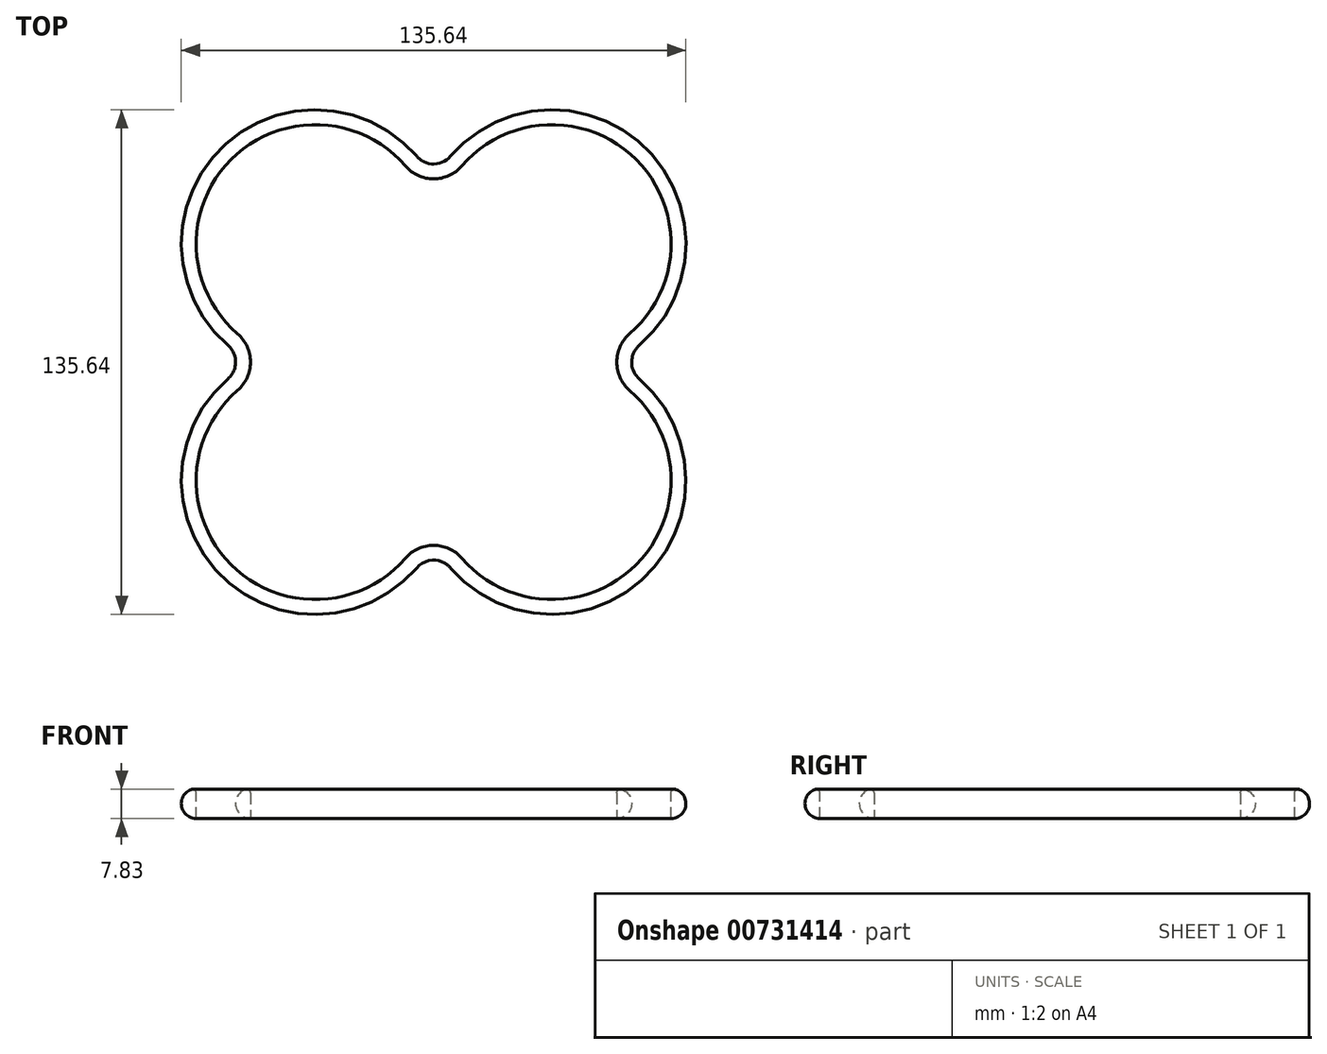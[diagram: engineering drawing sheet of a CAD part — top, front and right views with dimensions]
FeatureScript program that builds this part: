
annotation { "Feature Type Name" : "Feature", "Feature Type Description" : "" }
export const myFeature = defineFeature(function(context is Context, id is Id, definition is map)
    precondition{}
    {
        {
            var Q0;
            Q0=qCreatedBy(makeId("Top.planeOp"),FACE);
            var sketch = newSketch(context, id + "F0", { "sketchPlane" : qUnion([Q0])});
            skLineSegment(sketch, "E0", {"start": v(-31.82, -31.82) * mm, "end": v(31.82, 31.82) * mm, "construction": true});
            skLineSegment(sketch, "E1", {"start": v(-31.82, 31.82) * mm, "end": v(31.82, -31.82) * mm, "construction": true});
            skArc(sketch, "E2", {"start": v(-7.58, 52.7) * mm, "mid": v(-54.45, 54.45) * mm, "end": v(-52.7, 7.58) * mm});
            skArc(sketch, "E3", {"start": v(-52.7, -7.58) * mm, "mid": v(-54.45, -54.45) * mm, "end": v(-7.58, -52.7) * mm});
            skArc(sketch, "E4.trimOffspring", {"start": v(52.7, 7.58) * mm, "mid": v(54.45, 54.45) * mm, "end": v(7.58, 52.7) * mm});
            skArc(sketch, "E5.trimOffspring", {"start": v(7.58, -52.7) * mm, "mid": v(54.45, -54.45) * mm, "end": v(52.7, -7.58) * mm});
            skPoint(sketch, "E6.visualSharp", {"position": v(0, 35.21) * mm});
            skArc(sketch, "E6.filletArc", {"start": v(-7.58, 52.7) * mm, "mid": v(0, 49.23) * mm, "end": v(7.58, 52.7) * mm});
            skPoint(sketch, "E7.visualSharp", {"position": v(35.21, 0) * mm});
            skArc(sketch, "E7.filletArc", {"start": v(52.7, 7.58) * mm, "mid": v(49.23, 0) * mm, "end": v(52.7, -7.58) * mm});
            skPoint(sketch, "E8.visualSharp", {"position": v(-35.21, 0) * mm});
            skArc(sketch, "E8.filletArc", {"start": v(-52.7, -7.58) * mm, "mid": v(-49.23, 0) * mm, "end": v(-52.7, 7.58) * mm});
            skPoint(sketch, "E9.visualSharp", {"position": v(0, -35.21) * mm});
            skArc(sketch, "E9.filletArc", {"start": v(7.58, -52.7) * mm, "mid": v(0, -49.23) * mm, "end": v(-7.58, -52.7) * mm});
            skSolve(sketch);
        }
        {
            var Q0;
            Q0=qCreatedBy(makeId("Front.planeOp"),FACE);
            var sketch = newSketch(context, id + "F1", { "sketchPlane" : qUnion([Q0])});
            skPoint(sketch, "E10.0", {"position": v(-49.23, 0) * mm});
            skLineSegment(sketch, "E11", {"start": v(-49.23, 0) * mm, "end": v(-49.23, 8) * mm});
            skArc(sketch, "E12", {"start": v(-49.23, 8) * mm, "mid": v(-53.23, 4) * mm, "end": v(-49.23, 0) * mm});
            skSolve(sketch);
        }
        {
            var Q0;
            Q0=makeQuery(id+"F1.imprint","IMPRINT",FACE,{"disambiguationData":[TD([[makeQuery(id+"F1.imprint","IMPRINT",EDGE,{"derivedFrom":sQuery(id+"F1.wireOp",EDGE,"E11")}),1.0]])]});
            var Q1;
            Q1=sQuery(id+"F0.wireOp",EDGE,"E2");
            var Q2;
            Q2=sQuery(id+"F0.wireOp",EDGE,"E8.filletArc");
            var Q3;
            Q3=sQuery(id+"F0.wireOp",EDGE,"E3");
            var Q4;
            Q4=sQuery(id+"F0.wireOp",EDGE,"E6.filletArc");
            var Q5;
            Q5=sQuery(id+"F0.wireOp",EDGE,"E4.trimOffspring");
            var Q6;
            Q6=sQuery(id+"F0.wireOp",EDGE,"E7.filletArc");
            var Q7;
            Q7=sQuery(id+"F0.wireOp",EDGE,"E5.trimOffspring");
            var Q8;
            Q8=sQuery(id+"F0.wireOp",EDGE,"E9.filletArc");
            sweep(context, id + "F2", {"profiles" : qUnion([Q0]), "path" : qUnion([Q1, Q2, Q3, Q4, Q5, Q6, Q7, Q8])});
        }
        {
            var Q0;
            {var subQ0=sQuery(id+"F1.wireOp",EDGE,"kZlsNxFn-1mJC-PIbD-vrsf-6Qzc6ESqk09n");var subQ1=sQuery(id+"F1.wireOp",EDGE,"E11");var subQ2=sQuery(id+"F0.wireOp",EDGE,"E3");Q0=makeQuery(id+"F2.opSweep","SWEPT_EDGE",EDGE,{"disambiguationData":[OSD([subQ2,subQ1,subQ0]),TDD([subQ2,makeQuery(id+"F1.imprint","INTERSECT",VERTEX,{"disambiguationData":[OD(1.0)],"derivedFrom":[subQ1,subQ0]})])]});}
            fillet(context, id + "F3", {"entities" : qUnion([Q0]), "radius" : 1 * mm, "tangentPropagation" : true, "allowEdgeOverflow" : false});
        }
    });
